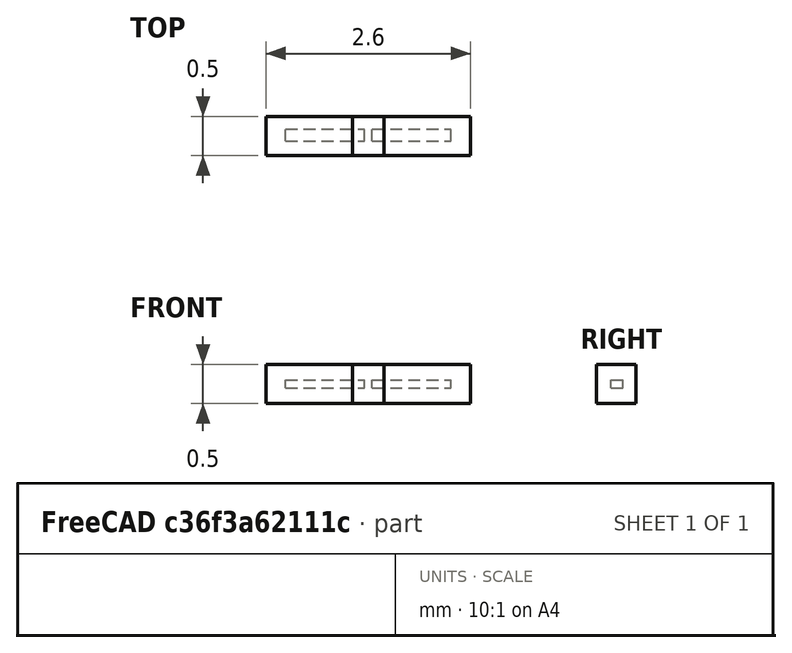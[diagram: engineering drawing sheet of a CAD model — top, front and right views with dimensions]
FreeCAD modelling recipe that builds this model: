
FCSTD DOCUMENT  (FreeCAD 1.0R39109 (Git))
Label: hull-1
License: All rights reserved
LicenseURL: https://en.wikipedia.org/wiki/All_rights_reserved
objects: Part::Feature×6, Part::Box×4, Part::FeaturePython×3, App::DocumentObjectGroupPython×2
note: 13 computed .brp shape members not serialized (recipe doc carries the construction recipe); baked Part::Feature solids carry a one-line shape summary decoded from their .brp

FEATURE [Part::Box] Box  label="hullWall1"
  AttacherType = Attacher::AttachEngine3D
  Height = 0.1
  Length = 1
  Placement = pos=(0,-0.075,-0.05) rot=(0,0,1;0rad)
  Width = 0.15
FEATURE [Part::Box] Box001  label="hullWall2"
  AttacherType = Attacher::AttachEngine3D
  Height = 0.1
  Length = 1
  Placement = pos=(-1.1,-0.075,-0.05) rot=(0,0,1;0rad)
  Width = 0.15
FEATURE [Part::Feature] Face  label="outlet"
  Placement = pos=(-1.5,-0.5,-0.5) rot=(0,0,1;0rad)
  shape: bbox 2e-07 x 1 x 1 mm, 1 faces, 0 solids (baked)
FEATURE [Part::Feature] Face001  label="inlet"
  Placement = pos=(-1.5,-0.5,-0.5) rot=(0,0,1;0rad)
  shape: bbox 2e-07 x 1 x 1 mm, 1 faces, 0 solids (baked)
FEATURE [Part::Feature] Face002  label="front"
  Placement = pos=(-1.5,-0.5,-0.5) rot=(0,0,1;0rad)
  shape: bbox 5 x 2e-07 x 1 mm, 1 faces, 0 solids (baked)
FEATURE [Part::Feature] Face003  label="back"
  Placement = pos=(-1.5,-0.5,-0.5) rot=(0,0,1;0rad)
  shape: bbox 5 x 2e-07 x 1 mm, 1 faces, 0 solids (baked)
FEATURE [Part::Feature] Face004  label="base"
  Placement = pos=(-1.5,-0.5,-0.5) rot=(0,0,1;0rad)
  shape: bbox 5 x 1 x 2e-07 mm, 1 faces, 0 solids (baked)
FEATURE [Part::Feature] Face005  label="atomosphere"
  Placement = pos=(-1.5,-0.5,-0.5) rot=(0,0,1;0rad)
  shape: bbox 5 x 1 x 2e-07 mm, 1 faces, 0 solids (baked)
FEATURE [Part::Box] Box002  label="overset1"
  AttacherType = Attacher::AttachEngine3D
  Height = 0.5
  Length = 1.5
  Placement = pos=(-0.25,-0.26,-0.25) rot=(0,0,1;0rad)
  Width = 0.5
FEATURE [Part::Box] Box003  label="overset2"
  AttacherType = Attacher::AttachEngine3D
  Height = 0.5
  Length = 1.5
  Placement = pos=(-1.35,-0.26,-0.25) rot=(0,0,1;0rad)
  Width = 0.5
FEATURE [Part::FeaturePython] CfdSolver  # WARN: FeaturePython — macro-defined, semantics opaque (R4)
  Parallel = true
  ParallelCores = 1
  ParallelMethod = 0
FEATURE [Part::FeaturePython] MeshRefinement  # WARN: FeaturePython — macro-defined, semantics opaque (R4)
  AllowDiscont = true
  CellSize = 0.051
  ExpansionRatio = 1.2
  FirstLayerHeight = 0
  Internal = false
  KeepCell = false
  NumberLayers = 1
  RefinementLevel = 0
  RefinementThickness = 0
  RemoveCell = false
  ShapeRefs = -> [Box]
  patchType = 1
FEATURE [Part::FeaturePython] MeshRefinement001  # WARN: FeaturePython — macro-defined, semantics opaque (R4)
  AllowDiscont = true
  CellSize = 0.051
  ExpansionRatio = 1.2
  FirstLayerHeight = 0
  Internal = false
  KeepCell = false
  NumberLayers = 1
  RefinementLevel = 0
  RefinementThickness = 0
  RemoveCell = false
  ShapeRefs = -> [Box002]
  patchType = 3
FEATURE [App::DocumentObjectGroupPython] CFDMesh  # scripted group (container) (typed FeaturePython)
  BaseCellSize = 0.025
  ElementDimension = 1
  FeatureAngle = 30
  Group = -> [MeshRefinement,MeshRefinement001]
  MeshUtility = 0
  ScaleToMeter = 1
  keepCellsIntersectingBoundary = false
  opt_featureSizeFactor = 0.4
  opt_maxNumIterations = 5
  opt_nSmoothNormals = 3
  opt_reCalculateNormals = true
  opt_relThicknessTol = 0.05
  optimiseLayer = false
  patchTypeSetting = false
  workflowControls = 0
FEATURE [App::DocumentObjectGroupPython] dexcsCfdAnalysis  # scripted group (container) (typed FeaturePython)
  Group = -> [CFDMesh,CfdSolver]
  IsActiveAnalysis = true
  NeedsCaseRewrite = true
  NeedsMeshRerun = true
  NeedsMeshRewrite = true
  PlotMaxnumber = 5000
  PlotMethodLast = false
